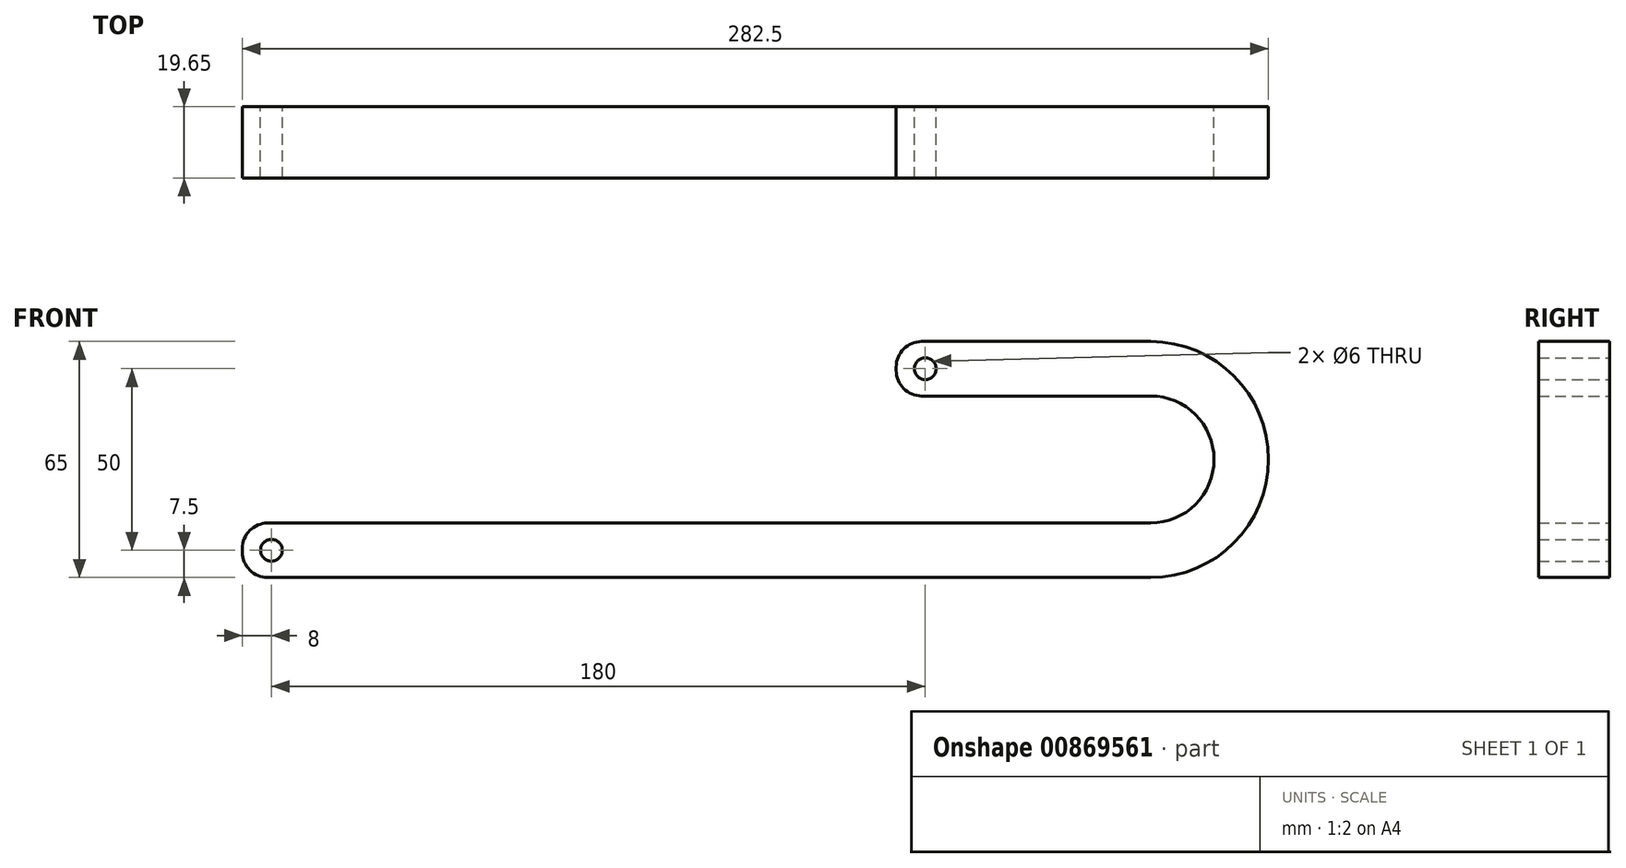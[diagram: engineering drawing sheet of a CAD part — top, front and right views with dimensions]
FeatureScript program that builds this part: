
annotation { "Feature Type Name" : "Feature", "Feature Type Description" : "" }
export const myFeature = defineFeature(function(context is Context, id is Id, definition is map)
    precondition{}
    {
        {
            var Q0;
            Q0=qCreatedBy(makeId("Front.planeOp"),FACE);
            var sketch = newSketch(context, id + "F0", { "sketchPlane" : qUnion([Q0])});
            skArc(sketch, "E0", {"start": v(0, -17.5) * mm, "mid": v(17.5, 0) * mm, "end": v(0, 17.5) * mm});
            skArc(sketch, "E1", {"start": v(0, -32.5) * mm, "mid": v(32.5, 0) * mm, "end": v(0, 32.5) * mm});
            skLineSegment(sketch, "E2", {"start": v(0, -32.5) * mm, "end": v(-250, -32.5) * mm});
            skLineSegment(sketch, "E3", {"start": v(0, -17.5) * mm, "end": v(-250, -17.5) * mm});
            skLineSegment(sketch, "E4", {"start": v(-250, -17.5) * mm, "end": v(-250, -32.5) * mm});
            skLineSegment(sketch, "E5", {"start": v(0, 17.5) * mm, "end": v(-70, 17.5) * mm});
            skLineSegment(sketch, "E6", {"start": v(0, 32.5) * mm, "end": v(-70, 32.5) * mm});
            skLineSegment(sketch, "E7", {"start": v(-70, 32.5) * mm, "end": v(-70, 17.5) * mm});
            skCircle(sketch, "E8", {"center": v(-62, 25) * mm, "radius": 3 * mm});
            skPoint(sketch, "E9", {"position": v(-70, 25) * mm});
            skCircle(sketch, "E10", {"center": v(-242, -25) * mm, "radius": 3 * mm});
            skPoint(sketch, "E11", {"position": v(-250, -25) * mm});
            skSolve(sketch);
        }
        {
            var Q0;
            Q0 = qSketchRegion(id + "F0", true);
            extrude(context, id + "F1", {"entities" : qUnion([Q0]), "depth" : 19.65 * mm, "offsetDistance" : 25 * mm});
        }
        {
            var Q0;
            Q0=makeQuery(id+"F1.opExtrude","SWEPT_EDGE",EDGE,{"disambiguationData":[OSD([sQuery(id+"F0.wireOp",EDGE,"E3"),sQuery(id+"F0.wireOp",EDGE,"E4")])]});
            var Q1;
            Q1=makeQuery(id+"F1.opExtrude","SWEPT_EDGE",EDGE,{"disambiguationData":[OSD([sQuery(id+"F0.wireOp",EDGE,"E2"),sQuery(id+"F0.wireOp",EDGE,"E4")])]});
            var Q2;
            Q2=makeQuery(id+"F1.opExtrude","SWEPT_EDGE",EDGE,{"disambiguationData":[OSD([sQuery(id+"F0.wireOp",EDGE,"E5"),sQuery(id+"F0.wireOp",EDGE,"E7")])]});
            var Q3;
            Q3=makeQuery(id+"F1.opExtrude","SWEPT_EDGE",EDGE,{"disambiguationData":[OSD([sQuery(id+"F0.wireOp",EDGE,"E6"),sQuery(id+"F0.wireOp",EDGE,"E7")])]});
            fillet(context, id + "F2", {"entities" : qUnion([Q0, Q1, Q2, Q3]), "tangentPropagation" : true, "radius" : 7 * mm, "defaultsChanged" : true, "vertexSettings" : [], "allowEdgeOverflow" : false});
        }
    });
